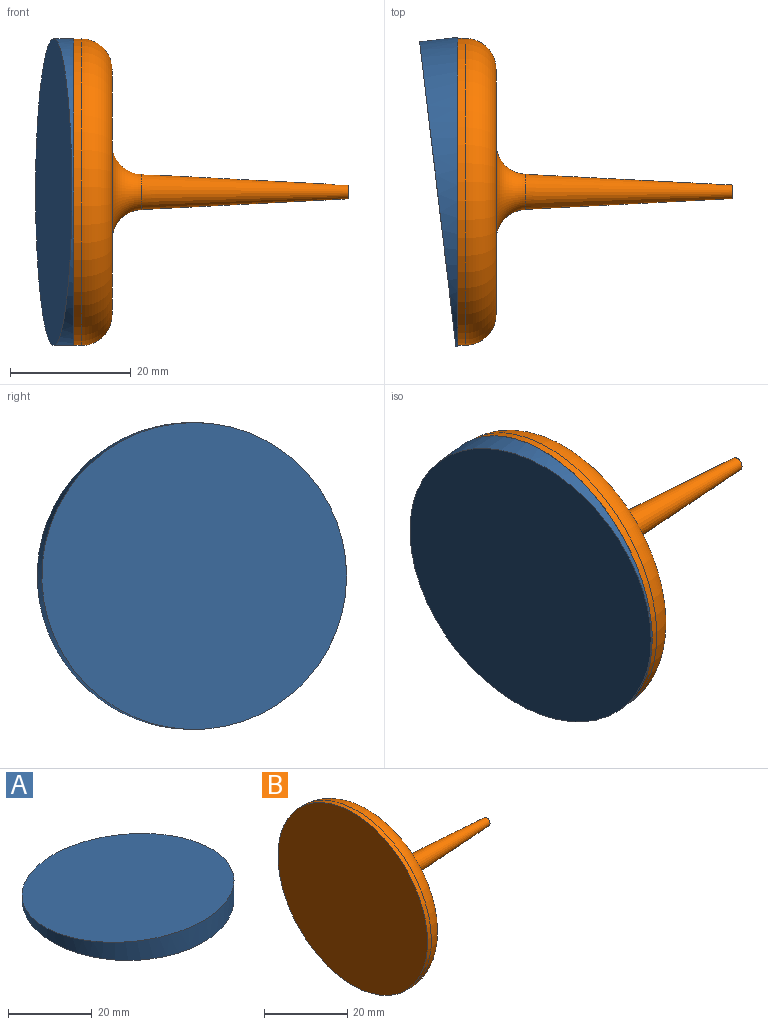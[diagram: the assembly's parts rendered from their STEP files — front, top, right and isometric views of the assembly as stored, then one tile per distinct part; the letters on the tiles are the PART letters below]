
ASSEMBLY  parts=2 mates=1
PART A: 3 faces, bbox 50.8x50.8x6.4 mm
  f0: cylinder r=25.4mm len=50.8mm, axis (0,0,-1), area 530mm2, adj f1,f2
  f1: plane 50.8x50.8mm, normal (0,0.12,0.99), area 2041.2mm2, adj f0
  f2: plane 50.8x50.8mm, normal (0,0,-1), area 2026.8mm2, adj f0
PART B: 7 faces, bbox 45.5x55x55 mm
  f0: cylinder r=25.4mm len=50.8mm, axis (-1,0,0), area 202.7mm2, adj f2,f6
  f1: plane 40.64x40.64mm, normal (1,0,0), area 1096.3mm2, adj f5,f6
  f2: plane 50.8x50.8mm, normal (-1,0,0), area 2026.8mm2, adj f0
  f3: cone r=3.17mm half-angle=3deg, axis (-1,0,0), area 436.8mm2, adj f4,f5
  f4: plane 2.25x2.25mm, normal (1,0,0), area 4mm2, adj f3
  f5: torus R=8mm, axis (1,0,0), area 233.9mm2, adj f1,f3
  f6: torus R=20.32mm, axis (1,0,0), area 1180.9mm2, adj f0,f1
PLACE A rot(axis=(-0.71,-0.04,-0.71),175.2deg) t=(5,33.67,52.86)mm
PLACE B t=(11.3,8.84,52.86)mm
MATE fastened A.f1 <-> B.f0  axis (1,0,0) through (11.3,8.84,52.86)mm
